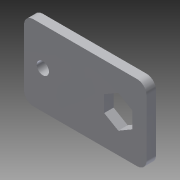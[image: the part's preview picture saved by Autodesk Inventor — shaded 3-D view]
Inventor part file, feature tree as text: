
AUTODESK INVENTOR PART (.ipt)
format: ipt  version: 2014 (Build 180170000, 170)  size: 95,232 bytes
history: native  units: in
note: dims shown in document units (in); Inventor stores cm internally (conversion verified against a paired STEP export)
features: extrude x1, fillet x1, sketch x1
ambient origin geometry x8: Origin, YZ Plane, XZ Plane, XY Plane, X Axis, Y Axis, Z Axis, Center Point
bodies: Solid1 (feature_tree)
feature tree (3):
  extrude  "Extrusion1"  Depth=1.0in
  fillet  "Fillet1"  Radius=0.163in
  sketch  "Sketch1"  dims[d0=1.625in d1=1.0in d2=0.163in d3=0.5in d4=0.25in d5=1.0in d6=0.375in d7=0.5in d8=0.125in d9=0.0in d10=0.125in]
